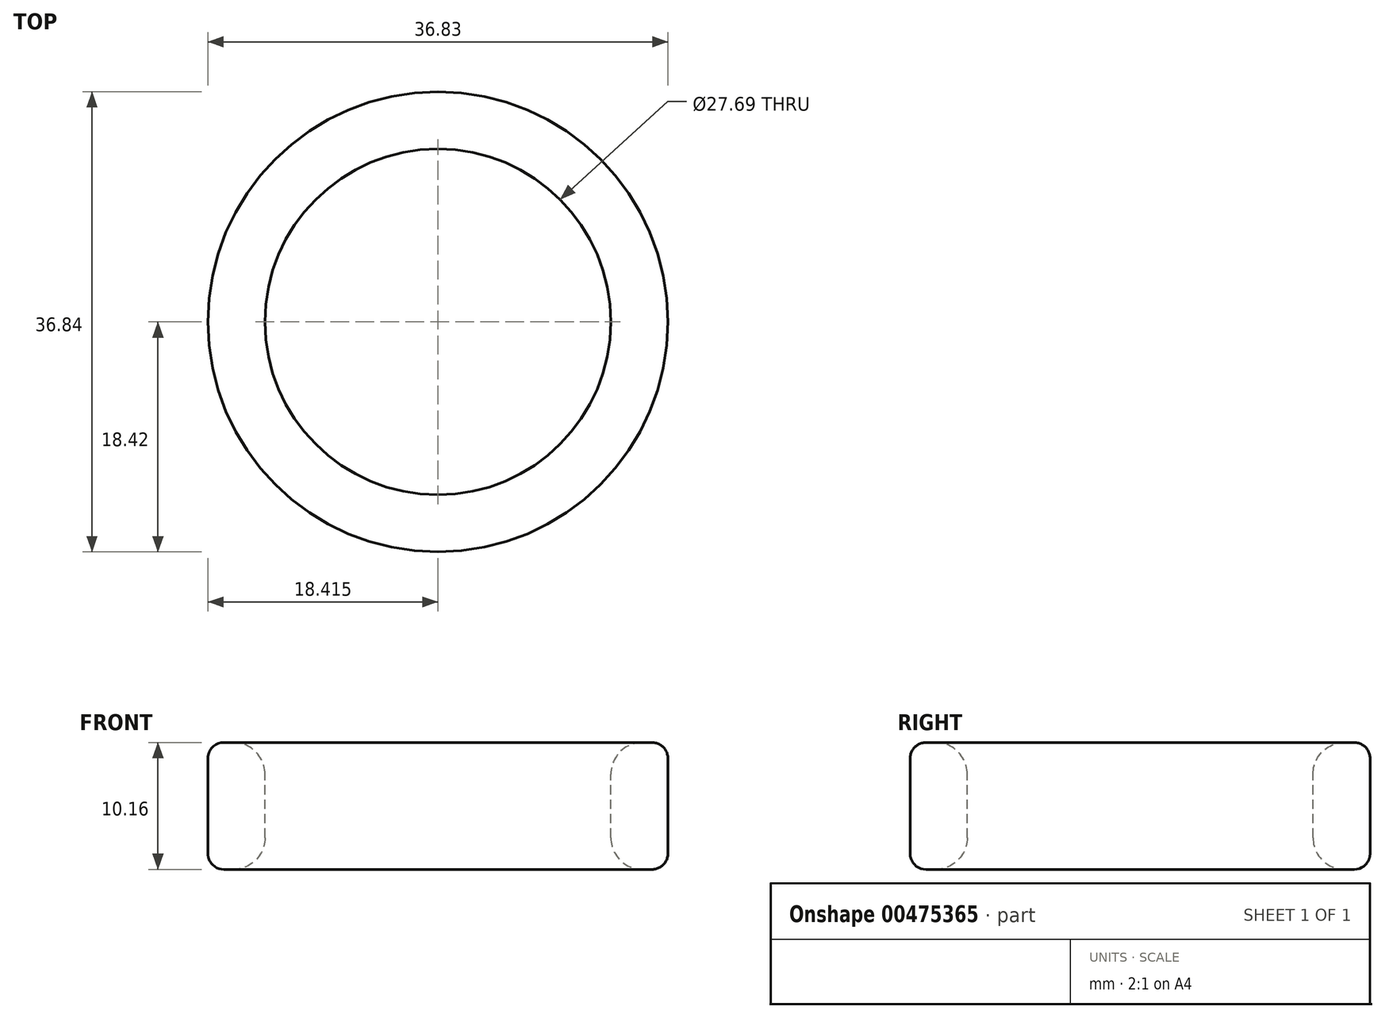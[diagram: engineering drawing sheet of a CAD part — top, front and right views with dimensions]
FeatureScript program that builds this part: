
annotation { "Feature Type Name" : "Feature", "Feature Type Description" : "" }
export const myFeature = defineFeature(function(context is Context, id is Id, definition is map)
    precondition{}
    {
        {
            var Q0;
            Q0=qCreatedBy(makeId("Front.planeOp"),FACE);
            var sketch = newSketch(context, id + "F0", { "sketchPlane" : qUnion([Q0])});
            skLineSegment(sketch, "E0.bottom", {"start": v(-18.78, 12.94) * mm, "end": v(18.05, 12.94) * mm});
            skLineSegment(sketch, "E0.top", {"start": v(-18.78, 2.78) * mm, "end": v(18.05, 2.78) * mm});
            skLineSegment(sketch, "E0.left", {"start": v(-18.78, 12.94) * mm, "end": v(-18.78, 2.78) * mm});
            skLineSegment(sketch, "E0.right", {"start": v(18.05, 12.94) * mm, "end": v(18.05, 2.78) * mm});
            skLineSegment(sketch, "E1", {"start": v(13.48, 12.94) * mm, "end": v(13.48, 2.78) * mm});
            skLineSegment(sketch, "E2", {"start": v(-0.37, 12.94) * mm, "end": v(-0.37, 2.78) * mm});
            skSolve(sketch);
        }
        {
            var Q0;
            {var subQ0=sQuery(id+"F0.wireOp",EDGE,"E0.right");Q0=makeQuery(id+"F0.imprint","IMPRINT",FACE,{"disambiguationData":[TD([[makeQuery(id+"F0.imprint","IMPRINT",EDGE,{"derivedFrom":subQ0}),-1.0]])]});}
            var Q1;
            Q1=sQuery(id+"F0.wireOp",EDGE,"E2");
            revolve(context, id + "F1", {"entities" : qUnion([Q0]), "axis" : qUnion([Q1]), "revolveType" : RevolveType.FULL});
        }
        {
            var Q0;
            Q0=makeQuery(id+"F1.opRevolve","SWEPT_EDGE",EDGE,{"disambiguationData":[OSD([sQuery(id+"F0.wireOp",EDGE,"E0.bottom"),sQuery(id+"F0.wireOp",EDGE,"E1")])]});
            var Q1;
            Q1=makeQuery(id+"F1.opRevolve","SWEPT_EDGE",EDGE,{"disambiguationData":[OSD([sQuery(id+"F0.wireOp",EDGE,"E0.top"),sQuery(id+"F0.wireOp",EDGE,"E1")])]});
            fillet(context, id + "F2", {"entities" : qUnion([Q0, Q1]), "radius" : 2.54 * mm, "tangentPropagation" : true, "allowEdgeOverflow" : false});
        }
        {
            var Q0;
            Q0=makeQuery(id+"F1.opRevolve","SWEPT_EDGE",EDGE,{"disambiguationData":[OSD([sQuery(id+"F0.wireOp",EDGE,"E0.bottom"),sQuery(id+"F0.wireOp",EDGE,"E0.right")])]});
            var Q1;
            Q1=makeQuery(id+"F1.opRevolve","SWEPT_EDGE",EDGE,{"disambiguationData":[OSD([sQuery(id+"F0.wireOp",EDGE,"E0.top"),sQuery(id+"F0.wireOp",EDGE,"E0.right")])]});
            fillet(context, id + "F3", {"entities" : qUnion([Q0, Q1]), "radius" : 1.27 * mm, "tangentPropagation" : true, "allowEdgeOverflow" : false});
        }
    });
